# Revit family: QF_Brema_IMF58A_IMF58W_cat
name_source: partatom
category: Specialty Equipment
revit_build: Autodesk Revit MEP 2012 (Build: 20110916_2132(x64)
units: mm (PartAtom-declared; Revit-internal decimal feet)

## types (2) — shared parameters
Apparent Power = 420 VA
Assembly Code = E1090320
BTUH = 0 W
Cold Water Connection Height = 196 mm  [stored 0.643045 ft]
Cold Water Maximum Pressure = 6.0 bar
Cold Water Minimum Pressure = 1.0 bar
Cold Water Size = 1"
Cold Water Size Radius = 1/2"
Conn Conduit = Yes
Cycle = 50 Hz
Depth = 580 mm  [stored 1.90289 ft]
Elec Conn Connection Height = 232 mm  [stored 0.761155 ft]
FL Amps = 0 A
Height = 797 mm  [stored 2.61483 ft]
Indirect Waste Connection Height = 151 mm  [stored 0.495407 ft]
Indirect Waste Radius = 1/2"
Indirect Waste Size = 1"
Manufacturer = BREMA
Max Overcurrent Protection = 10 A
Min Ckt Ampacity = 0 A
Phase = 1
Refrigerant Type = R404A
URL = www.bremaice.it
Volts = 230 V
Watts = 420 W
Weight = 54 kg
Width = 495 mm  [stored 1.62402 ft]

## per-type parameters (varying)
| type | Description |
| IMF58A | AUTOMATIC ICE CUBE MAKER AIR COOLED |
| IMF58W | AUTOMATIC ICE CUBE MAKER WATER COOLED |

note: column(s) folded — value = type name in every type: Model

note: [stored X ft] marks values corroborated as IEEE doubles in the binary element streams (Revit-internal decimal feet)

## geometry (parser evidence)
native form markers: Blend x7, Sweep x2
no freeform markers — native parametric forms only
